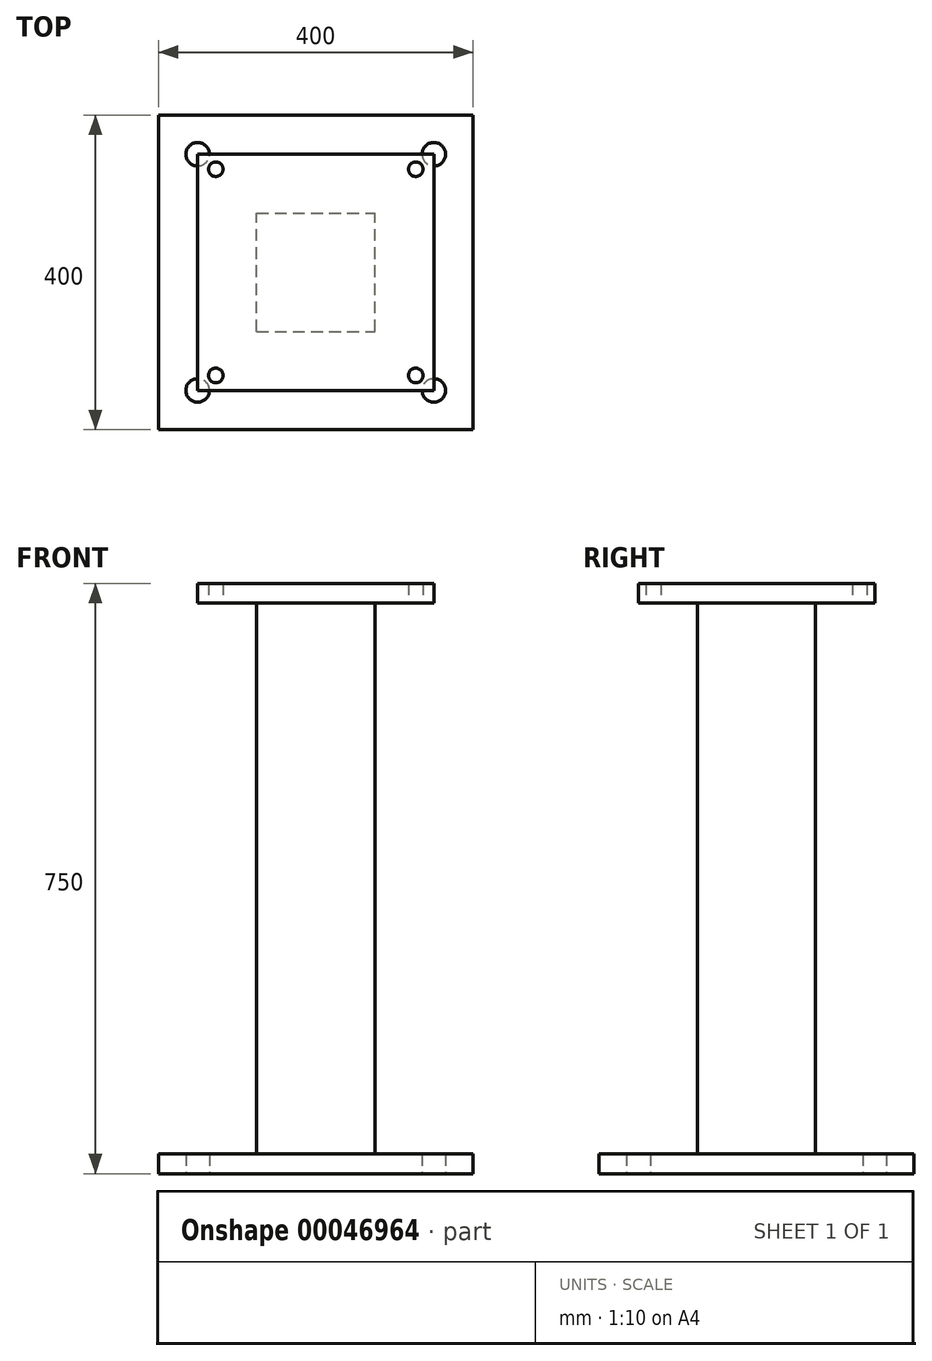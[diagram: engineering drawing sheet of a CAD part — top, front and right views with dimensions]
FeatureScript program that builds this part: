
annotation { "Feature Type Name" : "Feature", "Feature Type Description" : "" }
export const myFeature = defineFeature(function(context is Context, id is Id, definition is map)
    precondition{}
    {
        {
            var Q0;
            Q0=qCreatedBy(makeId("Top.planeOp"),FACE);
            var sketch = newSketch(context, id + "F0", { "sketchPlane" : qUnion([Q0])});
            skLineSegment(sketch, "E0.rect.bottom", {"start": v(-200, -200) * mm, "end": v(200, -200) * mm});
            skLineSegment(sketch, "E0.rect.top", {"start": v(-200, 200) * mm, "end": v(200, 200) * mm});
            skLineSegment(sketch, "E0.rect.left", {"start": v(-200, -200) * mm, "end": v(-200, 200) * mm});
            skLineSegment(sketch, "E0.rect.right", {"start": v(200, -200) * mm, "end": v(200, 200) * mm});
            skPoint(sketch, "E0.rect.middle", {"position": v(0, 0) * mm});
            skLineSegment(sketch, "E1.rect.bottom", {"start": v(-150, 150) * mm, "end": v(150, 150) * mm, "construction": true});
            skLineSegment(sketch, "E1.rect.top", {"start": v(-150, -150) * mm, "end": v(150, -150) * mm, "construction": true});
            skLineSegment(sketch, "E1.rect.left", {"start": v(-150, 150) * mm, "end": v(-150, -150) * mm, "construction": true});
            skLineSegment(sketch, "E1.rect.right", {"start": v(150, 150) * mm, "end": v(150, -150) * mm, "construction": true});
            skCircle(sketch, "E2", {"center": v(-150, 150) * mm, "radius": 15 * mm});
            skCircle(sketch, "E3", {"center": v(150, 150) * mm, "radius": 15 * mm});
            skCircle(sketch, "E4", {"center": v(150, -150) * mm, "radius": 15 * mm});
            skCircle(sketch, "E5", {"center": v(-150, -150) * mm, "radius": 15 * mm});
            skSolve(sketch);
        }
        {
            var Q0;
            Q0=makeQuery(id+"F0.imprint","IMPRINT",FACE,{"disambiguationData":[TD([[makeQuery(id+"F0.imprint","IMPRINT",EDGE,{"derivedFrom":sQuery(id+"F0.wireOp",EDGE,"E0.rect.bottom")}),1.0]])]});
            extrude(context, id + "F1", {"entities" : qUnion([Q0]), "depth" : 25 * mm});
        }
        {
            var Q0;
            Q0=makeQuery(id+"F1.opExtrude","CAP_FACE",FACE,{"disambiguationData":[OSD([sQuery(id+"F0.wireOp",EDGE,"E0.rect.bottom"),sQuery(id+"F0.wireOp",EDGE,"E0.rect.top"),sQuery(id+"F0.wireOp",EDGE,"E0.rect.left"),sQuery(id+"F0.wireOp",EDGE,"E0.rect.right"),sQuery(id+"F0.wireOp",EDGE,"E2"),sQuery(id+"F0.wireOp",EDGE,"E3"),sQuery(id+"F0.wireOp",EDGE,"E4"),sQuery(id+"F0.wireOp",EDGE,"E5")])],"isStart":false});
            var sketch = newSketch(context, id + "F2", { "sketchPlane" : qUnion([Q0])});
            skLineSegment(sketch, "E6.rect.bottom", {"start": v(-75, -75) * mm, "end": v(75, -75) * mm});
            skLineSegment(sketch, "E6.rect.top", {"start": v(-75, 75) * mm, "end": v(75, 75) * mm});
            skLineSegment(sketch, "E6.rect.left", {"start": v(-75, -75) * mm, "end": v(-75, 75) * mm});
            skLineSegment(sketch, "E6.rect.right", {"start": v(75, -75) * mm, "end": v(75, 75) * mm});
            skPoint(sketch, "E6.rect.middle", {"position": v(0, 0) * mm});
            skSolve(sketch);
        }
        {
            var Q0;
            Q0=qSketchRegion(id+"F2",true);
            extrude(context, id + "F3", {"entities" : qUnion([Q0]), "operationType" : NewBodyOperationType.ADD, "depth" : 700 * mm});
        }
        {
            var Q0;
            Q0=makeQuery(id+"F3.opExtrude","CAP_FACE",FACE,{"disambiguationData":[OSD([sQuery(id+"F2.wireOp",EDGE,"E6.rect.bottom"),sQuery(id+"F2.wireOp",EDGE,"E6.rect.top"),sQuery(id+"F2.wireOp",EDGE,"E6.rect.left"),sQuery(id+"F2.wireOp",EDGE,"E6.rect.right"),sQuery(id+"F2.wireOp",EDGE,"67ed4f4a-774a-4b06-a684-185f138b00ca.rect.bottom"),sQuery(id+"F2.wireOp",EDGE,"67ed4f4a-774a-4b06-a684-185f138b00ca.rect.top"),sQuery(id+"F2.wireOp",EDGE,"67ed4f4a-774a-4b06-a684-185f138b00ca.rect.left"),sQuery(id+"F2.wireOp",EDGE,"67ed4f4a-774a-4b06-a684-185f138b00ca.rect.right")])],"isStart":false});
            var sketch = newSketch(context, id + "F4", { "sketchPlane" : qUnion([Q0])});
            skLineSegment(sketch, "E7.rect.bottom", {"start": v(-150, 150) * mm, "end": v(150, 150) * mm});
            skLineSegment(sketch, "E7.rect.top", {"start": v(-150, -150) * mm, "end": v(150, -150) * mm});
            skLineSegment(sketch, "E7.rect.left", {"start": v(-150, 150) * mm, "end": v(-150, -150) * mm});
            skLineSegment(sketch, "E7.rect.right", {"start": v(150, 150) * mm, "end": v(150, -150) * mm});
            skPoint(sketch, "E7.rect.middle", {"position": v(0, 0) * mm});
            skLineSegment(sketch, "E8", {"start": v(-127, 131) * mm, "end": v(127, 131) * mm, "construction": true});
            skLineSegment(sketch, "E9", {"start": v(127, 131) * mm, "end": v(127, -131) * mm, "construction": true});
            skLineSegment(sketch, "E10", {"start": v(127, -131) * mm, "end": v(-127, -131) * mm, "construction": true});
            skLineSegment(sketch, "E11", {"start": v(-127, -131) * mm, "end": v(-127, 131) * mm, "construction": true});
            skCircle(sketch, "E12", {"center": v(-127, 131) * mm, "radius": 9.25 * mm});
            skCircle(sketch, "E13", {"center": v(127, 131) * mm, "radius": 9.25 * mm});
            skCircle(sketch, "E14", {"center": v(-127, -131) * mm, "radius": 9.25 * mm});
            skCircle(sketch, "E15", {"center": v(127, -131) * mm, "radius": 9.25 * mm});
            skSolve(sketch);
        }
        {
            var Q0;
            Q0=qSketchRegion(id+"F4",true);
            extrude(context, id + "F5", {"entities" : qUnion([Q0]), "operationType" : NewBodyOperationType.ADD, "depth" : 25 * mm});
        }
    });
